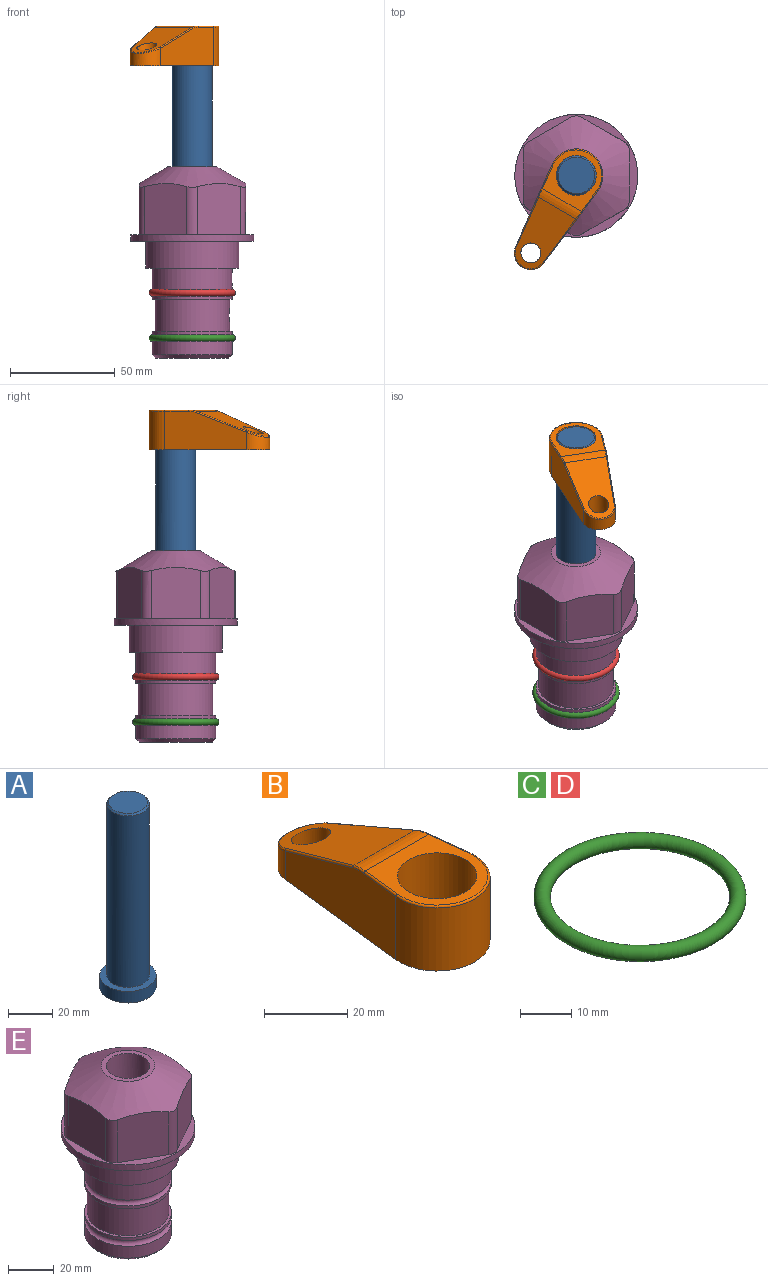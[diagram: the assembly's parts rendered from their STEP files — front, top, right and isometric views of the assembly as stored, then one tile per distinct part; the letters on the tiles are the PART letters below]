
ASSEMBLY  parts=5 mates=3
PART A: 6 faces, bbox 25.4x25.4x101.6 mm
  f0: plane 17.46x17.46mm, normal (0,0,1), area 239.5mm2, adj f5
  f1: plane 25.4x25.4mm, normal (0,0,-1), area 506.7mm2, adj f2
  f2: cylinder r=12.7mm len=25.4mm, axis (0,0,1), area 506.7mm2, adj f1,f3
  f3: plane 25.4x25.4mm, normal (0,0,1), area 221.7mm2, adj f2,f4
  f4: cylinder r=9.53mm len=94.46mm, axis (0,0,1), area 5653mm2, adj f3,f5
  f5: cone r=8.73mm half-angle=45deg, axis (0,0,-1), area 64.4mm2, adj f0,f4
PART B: 44 faces, bbox 27.5x64.5x19.1 mm
  f0: plane 2.3x0.95mm, normal (0,0,-1), area 1mm2, adj f25,f30,f34
  f1: plane 63.5x25.4mm, normal (0,0,-1), area 561.7mm2, adj f2,f3,f4,f5,f6,f7,f19,f20
  f2: cylinder r=12.7mm len=25.4mm, axis (0,0,-1), area 792.2mm2, adj f1,f3,f5,f13
  f3: plane 42.33x18.54mm, normal (0.99,0.11,0), area 647mm2, adj f1,f2,f4,f11,f12,f14
  f4: cylinder r=7.94mm len=15.78mm, axis (0,0,-1), area 158.6mm2, adj f1,f3,f5,f16
  f5: plane 42.33x18.54mm, normal (-0.99,0.11,0), area 647mm2, adj f1,f2,f4,f15,f17,f18
  f6: cylinder r=9.53mm len=19.05mm, axis (0,0,-1), area 1140.1mm2, adj f1,f8
  f7: cylinder r=4.76mm len=10.98mm, axis (0,0,-1), area 276.1mm2, adj f1,f9
  f8: plane 25.83x24.38mm, normal (0,0,1), area 262.2mm2, adj f6,f10,f11,f13,f15
  f9: plane 32.49x20.55mm, normal (0,0.34,0.94), area 489.9mm2, adj f7,f10,f14,f16,f18
  f10: cylinder r=12.7mm len=21.49mm, axis (-1,0,0), area 93.2mm2, adj f8,f9,f12,f17
  f11: cylinder r=0.51mm len=12.34mm, axis (0.11,-0.99,0), area 9.9mm2, adj f3,f8,f12,f13
  f12: bspline ~7.62x1.64mm, area 3.5mm2, adj f3,f10,f11,f14
  f13: torus R=12.19mm, axis (0,0,1), area 33.6mm2, adj f2,f8,f11,f15
  f14: cylinder r=0.51mm len=26.01mm, axis (0.1,-0.93,0.34), area 21.6mm2, adj f3,f9,f12,f16
  f15: cylinder r=0.51mm len=12.34mm, axis (0.11,0.99,0), area 9.9mm2, adj f5,f8,f13,f17
  f16: bspline ~15.78x7.05mm, area 15.7mm2, adj f4,f9,f14,f18
  f17: bspline ~7.62x1.64mm, area 3.5mm2, adj f5,f10,f15,f18
  f18: cylinder r=0.51mm len=26.01mm, axis (0.1,0.93,-0.34), area 21.6mm2, adj f5,f9,f16,f17
  f19: plane 21.6x14.29mm, normal (-0.99,-0.11,0), area 242.6mm2, adj f1,f26,f28,f34,f36,f38
  f20: plane 21.6x14.29mm, normal (0.99,-0.11,0), area 242.6mm2, adj f1,f27,f29,f37,f39,f41
  f21: cylinder r=12.7mm len=14.29mm, axis (0,0,-1), area 173.2mm2, adj f1,f26,f27,f30,f31,f33
  f22: cylinder r=7.94mm len=7.63mm, axis (0,0,-1), area 53.8mm2, adj f1,f28,f29,f42
  f23: plane 2.3x0.95mm, normal (0,0,-1), area 1mm2, adj f25,f33,f37
  f24: plane 17.94x12.32mm, normal (0,-0.34,-0.94), area 191.2mm2, adj f25,f38,f41,f42
  f25: cylinder r=9.53mm len=12.93mm, axis (-1,0,0), area 37.5mm2, adj f0,f23,f24,f31,f36,f39
  f26: cylinder r=1.59mm len=14.29mm, axis (0,0,-1), area 49mm2, adj f1,f19,f21,f32
  f27: cylinder r=1.59mm len=14.29mm, axis (0,0,-1), area 49mm2, adj f1,f20,f21,f35
  f28: cylinder r=1.59mm len=7.28mm, axis (0,0,-1), area 22.1mm2, adj f1,f19,f22,f40
  f29: cylinder r=1.59mm len=7.28mm, axis (0,0,-1), area 22.1mm2, adj f1,f20,f22,f43
  f30: torus R=14.29mm, axis (0,0,1), area 5.8mm2, adj f0,f21,f31,f32
  f31: bspline ~11.06x2.73mm, area 20.8mm2, adj f21,f25,f30,f33
  f32: sphere r=1.59mm, area 5.4mm2, adj f26,f30,f34
  f33: torus R=14.29mm, axis (0,0,1), area 5.8mm2, adj f21,f23,f31,f35
  f34: cylinder r=1.59mm len=1.68mm, axis (-0.11,0.99,0), area 2.4mm2, adj f0,f19,f32,f36
  f35: sphere r=1.59mm, area 5.4mm2, adj f27,f33,f37
  f36: bspline ~5.82x2.33mm, area 7.7mm2, adj f19,f25,f34,f38
  f37: cylinder r=1.59mm len=1.68mm, axis (0.11,0.99,0), area 2.4mm2, adj f20,f23,f35,f39
  f38: cylinder r=1.59mm len=18.33mm, axis (0.1,-0.93,0.34), area 46.7mm2, adj f19,f24,f36,f40
  f39: bspline ~5.82x2.33mm, area 7.7mm2, adj f20,f25,f37,f41
  f40: sphere r=1.59mm, area 3.6mm2, adj f28,f38,f42
  f41: cylinder r=1.59mm len=18.33mm, axis (0.1,0.93,-0.34), area 46.7mm2, adj f20,f24,f39,f43
  f42: bspline ~8.31x1.84mm, area 15.3mm2, adj f22,f24,f40,f43
  f43: sphere r=1.59mm, area 3.6mm2, adj f29,f41,f42
PART C: 1 faces, bbox 44.7x44.7x3.2 mm
  f0: torus R=19.05mm, axis (0,0,1), area 1193.9mm2
PART D: same geometry as C
PART E: 36 faces, bbox 58.7x58.7x91.2 mm
  f0: cylinder r=17.78mm len=35.56mm, axis (0,0,1), area 1670.8mm2, adj f23,f24,f31
  f1: cylinder r=19.05mm len=38.1mm, axis (0,0,1), area 1191.9mm2, adj f26,f27,f30
  f2: plane 58.66x58.66mm, normal (0,0,-1), area 1150.6mm2, adj f3,f28
  f3: cylinder r=29.33mm len=58.66mm, axis (0,0,-1), area 585.1mm2, adj f2,f4
  f4: plane 58.66x58.66mm, normal (0,0,1), area 475.9mm2, adj f3,f5,f6,f7,f8,f9,f10,f11
  f5: plane 24.5x20.32mm, normal (-0.5,0.87,0), area 562.8mm2, adj f4,f15,f16,f17
  f6: plane 24.5x20.32mm, normal (0.5,0.87,0), area 562.8mm2, adj f4,f14,f15,f17
  f7: plane 24.5x23.48mm, normal (1,0,0), area 562.8mm2, adj f4,f13,f14,f17
  f8: plane 24.5x20.32mm, normal (0.5,-0.87,0), area 562.8mm2, adj f4,f12,f13,f17
  f9: plane 24.5x20.32mm, normal (-0.5,-0.87,0), area 562.8mm2, adj f4,f11,f12,f17
  f10: plane 24.5x23.48mm, normal (-1,0,0), area 562.8mm2, adj f4,f11,f16,f17
  f11: cylinder r=5.08mm len=23.01mm, axis (0,0,-1), area 121.2mm2, adj f4,f9,f10,f17
  f12: cylinder r=5.08mm len=23.01mm, axis (0,0,-1), area 121.2mm2, adj f4,f8,f9,f17
  f13: cylinder r=5.08mm len=23.01mm, axis (0,0,-1), area 121.2mm2, adj f4,f7,f8,f17
  f14: cylinder r=5.08mm len=23.01mm, axis (0,0,-1), area 121.2mm2, adj f4,f6,f7,f17
  f15: cylinder r=5.08mm len=23.01mm, axis (0,0,-1), area 121.2mm2, adj f4,f5,f6,f17
  f16: cylinder r=5.08mm len=23.01mm, axis (0,0,-1), area 121.2mm2, adj f4,f5,f10,f17
  f17: cone r=11.73mm half-angle=60deg, axis (0,0,-1), area 2071.8mm2, adj f5,f6,f7,f8,f9,f10,f11,f12
  f18: plane 23.46x23.46mm, normal (0,0,1), area 147.4mm2, adj f17,f35
  f19: plane 34.93x34.93mm, normal (0,0,-1), area 958mm2, adj f29
  f20: cylinder r=19.05mm len=38.1mm, axis (0,0,1), area 760.1mm2, adj f21,f29
  f21: torus R=19.05mm, axis (0,0,1), area 565.3mm2, adj f20,f22
  f22: cylinder r=19.05mm len=38.1mm, axis (0,0,1), area 190mm2, adj f21,f23
  f23: plane 38.1x38.1mm, normal (0,0,1), area 146.9mm2, adj f0,f22
  f24: plane 38.1x38.1mm, normal (0,0,-1), area 146.9mm2, adj f0,f25
  f25: cylinder r=19.05mm len=38.1mm, axis (0,0,1), area 190mm2, adj f24,f26
  f26: torus R=19.05mm, axis (0,0,1), area 565.3mm2, adj f1,f25
  f27: plane 44.45x44.45mm, normal (0,0,-1), area 411.7mm2, adj f1,f28
  f28: cylinder r=22.23mm len=44.45mm, axis (0,0,1), area 1773.5mm2, adj f2,f27
  f29: cone r=19.05mm half-angle=45deg, axis (0,0,1), area 257.5mm2, adj f19,f20
  f30: cylinder r=3.17mm len=6.75mm, axis (-1,0,0), area 128mm2, adj f1,f33
  f31: cylinder r=3.17mm len=6.35mm, axis (-1,0,0), area 102.5mm2, adj f0,f33
  f32: plane 25.4x25.4mm, normal (0,0,1), area 506.7mm2, adj f33
  f33: cylinder r=12.7mm len=66.42mm, axis (0,0,-1), area 5236.2mm2, adj f30,f31,f32,f34
  f34: cone r=9.53mm half-angle=30deg, axis (0,0,-1), area 443.4mm2, adj f33,f35
  f35: cylinder r=9.53mm len=19.05mm, axis (0,0,-1), area 849mm2, adj f18,f34
PLACE A rot(axis=(0,0,-1),120.4deg) t=(0,0,29.16)mm
PLACE B rot(axis=(0,0,1),149.6deg) t=(0,0,83.77)mm
PLACE C t=(0,0,-21.59)mm
PLACE D at identity
PLACE E at identity fixed
MATE fastened C.f0 <-> E.f0  axis (0,0,1) through (0,0,-46.1)mm
MATE cylindrical A.f2 <-> E.f0  axis (0,0,1) through (0,0,54.8)mm
MATE fastened B.f2 <-> A.f2  axis (0,0,1) through (0,0,102.82)mm
